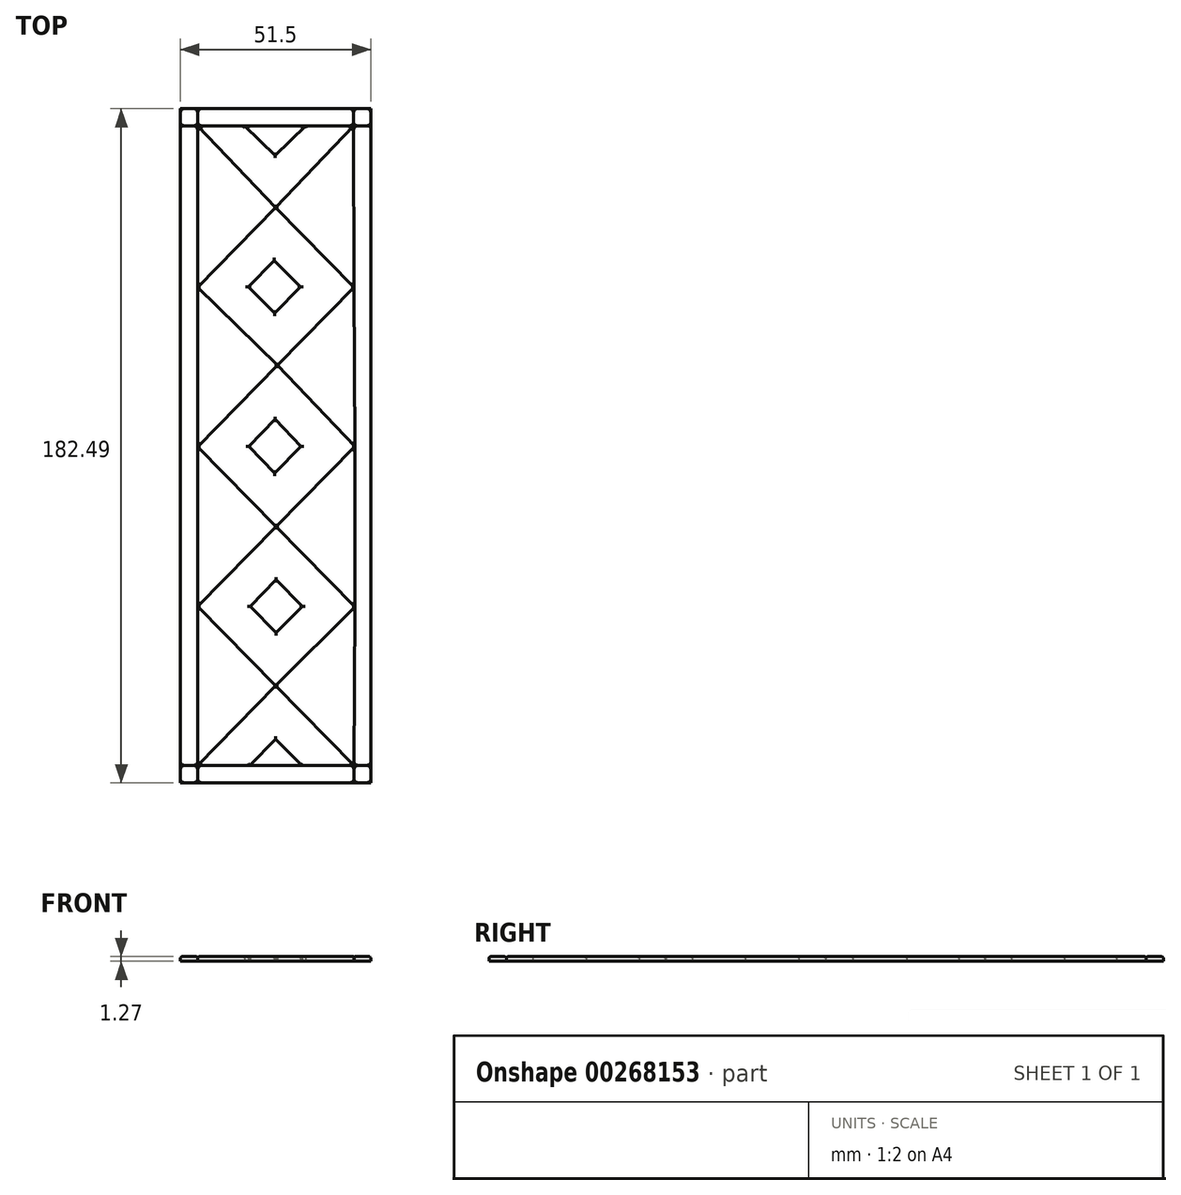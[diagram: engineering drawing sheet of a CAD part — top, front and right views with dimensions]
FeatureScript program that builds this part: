
annotation { "Feature Type Name" : "Feature", "Feature Type Description" : "" }
export const myFeature = defineFeature(function(context is Context, id is Id, definition is map)
    precondition{}
    {
        {
            var Q0;
            Q0=qCreatedBy(makeId("Top.planeOp"),FACE);
            var sketch = newSketch(context, id + "F0", { "sketchPlane" : qUnion([Q0])});
            skLineSegment(sketch, "E0.left", {"start": v(0, 0) * mm, "end": v(0, -4.69) * mm});
            skLineSegment(sketch, "E0.right", {"start": v(51.5, 0) * mm, "end": v(51.5, -4.69) * mm});
            skLineSegment(sketch, "E1.left", {"start": v(0, -182.5) * mm, "end": v(0, -177.8) * mm});
            skLineSegment(sketch, "E1.right", {"start": v(51.5, -182.5) * mm, "end": v(51.5, -177.8) * mm});
            skLineSegment(sketch, "E2.bottom", {"start": v(0, 0) * mm, "end": v(4.69, 0) * mm});
            skLineSegment(sketch, "E2.top", {"start": v(0, -182.5) * mm, "end": v(4.69, -182.5) * mm});
            skLineSegment(sketch, "E3.bottom", {"start": v(46.81, 0) * mm, "end": v(51.5, 0) * mm});
            skLineSegment(sketch, "E3.top", {"start": v(46.93, -182.5) * mm, "end": v(51.61, -182.5) * mm});
            skPoint(sketch, "E4.endSnap0", {"position": v(47.2, -91.38) * mm});
            skLineSegment(sketch, "E5", {"start": v(4.69, -177.8) * mm, "end": v(0, -177.8) * mm});
            skLineSegment(sketch, "E6", {"start": v(46.93, -177.8) * mm, "end": v(4.69, -177.8) * mm});
            skLineSegment(sketch, "E7", {"start": v(46.93, -177.8) * mm, "end": v(51.5, -177.8) * mm});
            skLineSegment(sketch, "E8", {"start": v(4.69, -4.69) * mm, "end": v(4.69, 0) * mm});
            skLineSegment(sketch, "E9", {"start": v(4.69, -177.8) * mm, "end": v(4.69, -182.5) * mm});
            skLineSegment(sketch, "E10", {"start": v(4.69, -48.3) * mm, "end": v(4.69, -4.69) * mm});
            skLineSegment(sketch, "E11", {"start": v(4.69, -91.46) * mm, "end": v(4.69, -48.3) * mm});
            skLineSegment(sketch, "E12", {"start": v(4.69, -134.64) * mm, "end": v(4.69, -91.46) * mm});
            skLineSegment(sketch, "E13", {"start": v(4.69, -177.8) * mm, "end": v(4.69, -134.64) * mm});
            skLineSegment(sketch, "E14", {"start": v(46.93, -177.8) * mm, "end": v(47.18, -134.78) * mm});
            skLineSegment(sketch, "E15", {"start": v(47.2, -91.38) * mm, "end": v(47.18, -134.78) * mm});
            skLineSegment(sketch, "E16", {"start": v(47.2, -91.38) * mm, "end": v(46.93, -48.3) * mm});
            skLineSegment(sketch, "E17", {"start": v(46.81, -4.69) * mm, "end": v(46.93, -48.3) * mm});
            skLineSegment(sketch, "E18", {"start": v(46.81, -4.69) * mm, "end": v(46.81, 0) * mm});
            skLineSegment(sketch, "E19", {"start": v(46.93, -177.8) * mm, "end": v(46.93, -182.5) * mm});
            skLineSegment(sketch, "E20", {"start": v(0, -4.69) * mm, "end": v(0, -177.8) * mm});
            skLineSegment(sketch, "E21", {"start": v(0, -4.69) * mm, "end": v(4.69, -4.69) * mm});
            skLineSegment(sketch, "E22", {"start": v(4.69, -4.69) * mm, "end": v(46.81, -4.69) * mm});
            skLineSegment(sketch, "E23", {"start": v(46.81, -4.69) * mm, "end": v(51.5, -4.69) * mm});
            skLineSegment(sketch, "E24", {"start": v(4.69, 0) * mm, "end": v(46.81, 0) * mm});
            skLineSegment(sketch, "E25", {"start": v(4.69, -182.5) * mm, "end": v(46.93, -182.5) * mm});
            skLineSegment(sketch, "E26", {"start": v(51.5, -177.8) * mm, "end": v(51.5, -4.69) * mm});
            skLineSegment(sketch, "E27", {"start": v(25.6, -84.07) * mm, "end": v(18.45, -91.38) * mm});
            skLineSegment(sketch, "E28", {"start": v(18.45, -91.38) * mm, "end": v(25.5, -98.63) * mm});
            skLineSegment(sketch, "E29", {"start": v(25.5, -98.63) * mm, "end": v(32.62, -91.35) * mm});
            skLineSegment(sketch, "E30", {"start": v(32.62, -91.35) * mm, "end": v(25.6, -84.07) * mm});
            skLineSegment(sketch, "E31", {"start": v(25.39, -41.05) * mm, "end": v(18.4, -48.2) * mm});
            skLineSegment(sketch, "E32", {"start": v(18.4, -48.2) * mm, "end": v(25.52, -55.3) * mm});
            skLineSegment(sketch, "E33", {"start": v(25.52, -55.3) * mm, "end": v(32.47, -48.2) * mm});
            skLineSegment(sketch, "E34", {"start": v(32.47, -48.2) * mm, "end": v(25.39, -41.05) * mm});
            skLineSegment(sketch, "E35", {"start": v(26.21, -69.46) * mm, "end": v(4.69, -48.3) * mm});
            skLineSegment(sketch, "E36", {"start": v(26.21, -69.46) * mm, "end": v(46.93, -48.3) * mm});
            skLineSegment(sketch, "E37", {"start": v(46.93, -48.3) * mm, "end": v(25.8, -26.7) * mm});
            skLineSegment(sketch, "E38", {"start": v(4.69, -48.3) * mm, "end": v(25.8, -26.7) * mm});
            skPoint(sketch, "E39.endSnap0", {"position": v(2.34, -4.69) * mm});
            skLineSegment(sketch, "E40", {"start": v(25.8, -26.7) * mm, "end": v(4.69, -4.69) * mm});
            skLineSegment(sketch, "E41", {"start": v(25.8, -26.7) * mm, "end": v(46.81, -4.69) * mm});
            skLineSegment(sketch, "E42", {"start": v(17.31, -4.69) * mm, "end": v(25.58, -12.61) * mm});
            skLineSegment(sketch, "E43", {"start": v(25.58, -12.61) * mm, "end": v(33.84, -4.69) * mm});
            skLineSegment(sketch, "E44", {"start": v(17.31, -4.69) * mm, "end": v(33.84, -4.69) * mm});
            skLineSegment(sketch, "E45", {"start": v(25.93, -113.12) * mm, "end": v(47.2, -91.38) * mm});
            skLineSegment(sketch, "E46", {"start": v(26.21, -69.46) * mm, "end": v(4.69, -91.46) * mm});
            skLineSegment(sketch, "E47", {"start": v(25.93, -113.12) * mm, "end": v(4.69, -91.46) * mm});
            skLineSegment(sketch, "E48", {"start": v(26.21, -69.46) * mm, "end": v(47.2, -91.38) * mm});
            skLineSegment(sketch, "E49", {"start": v(25.92, -127.5) * mm, "end": v(32.99, -134.72) * mm});
            skLineSegment(sketch, "E50", {"start": v(32.99, -134.72) * mm, "end": v(25.88, -141.87) * mm});
            skLineSegment(sketch, "E51", {"start": v(25.88, -141.87) * mm, "end": v(18.82, -134.67) * mm});
            skLineSegment(sketch, "E52", {"start": v(18.82, -134.67) * mm, "end": v(25.92, -127.5) * mm});
            skLineSegment(sketch, "E53", {"start": v(47.18, -134.78) * mm, "end": v(25.8, -156.22) * mm});
            skLineSegment(sketch, "E54", {"start": v(4.69, -134.64) * mm, "end": v(25.8, -156.22) * mm});
            skLineSegment(sketch, "E55", {"start": v(25.93, -113.12) * mm, "end": v(4.69, -134.64) * mm});
            skLineSegment(sketch, "E56", {"start": v(25.93, -113.12) * mm, "end": v(47.18, -134.78) * mm});
            skLineSegment(sketch, "E57", {"start": v(18.77, -177.8) * mm, "end": v(32.85, -177.8) * mm});
            skLineSegment(sketch, "E58", {"start": v(25.8, -170.61) * mm, "end": v(18.77, -177.8) * mm});
            skLineSegment(sketch, "E59", {"start": v(25.8, -170.61) * mm, "end": v(32.85, -177.8) * mm});
            skLineSegment(sketch, "E60", {"start": v(25.8, -156.22) * mm, "end": v(4.69, -177.8) * mm});
            skLineSegment(sketch, "E61", {"start": v(25.8, -156.22) * mm, "end": v(46.93, -177.8) * mm});
            skSolve(sketch);
        }
        {
            var Q0;
            {var subQ5=sQuery(id+"F0.wireOp",EDGE,"E2.bottom");Q0=makeQuery(id+"F0.imprint","IMPRINT",FACE,{"disambiguationData":[TD([[makeQuery(id+"F0.imprint","IMPRINT",EDGE,{"derivedFrom":subQ5}),-1.0]])]});}
            var Q1;
            {var subQ5=sQuery(id+"F0.wireOp",EDGE,"E3.bottom");Q1=makeQuery(id+"F0.imprint","IMPRINT",FACE,{"disambiguationData":[TD([[makeQuery(id+"F0.imprint","IMPRINT",EDGE,{"derivedFrom":subQ5}),-1.0]])]});}
            var Q2;
            {var subQ5=sQuery(id+"F0.wireOp",EDGE,"E2.top");Q2=makeQuery(id+"F0.imprint","IMPRINT",FACE,{"disambiguationData":[TD([[makeQuery(id+"F0.imprint","IMPRINT",EDGE,{"derivedFrom":subQ5}),1.0]])]});}
            var Q3;
            {var subQ5=sQuery(id+"F0.wireOp",EDGE,"E3.top");Q3=makeQuery(id+"F0.imprint","IMPRINT",FACE,{"disambiguationData":[TD([[makeQuery(id+"F0.imprint","IMPRINT",EDGE,{"derivedFrom":subQ5}),1.0]])]});}
            var Q4;
            Q4=makeQuery(id+"F0.imprint","IMPRINT",FACE,{"disambiguationData":[TD([[makeQuery(id+"F0.imprint","IMPRINT",EDGE,{"derivedFrom":sQuery(id+"F0.wireOp",EDGE,"E42")}),1.0]])]});
            var Q5;
            Q5=makeQuery(id+"F0.imprint","IMPRINT",FACE,{"disambiguationData":[TD([[makeQuery(id+"F0.imprint","IMPRINT",EDGE,{"derivedFrom":sQuery(id+"F0.wireOp",EDGE,"E57")}),1.0]])]});
            extrude(context, id + "F1", {"entities" : qUnion([Q0, Q1, Q2, Q3, Q4, Q5]), "depth" : 1.27 * mm});
        }
        {
            var Q0;
            Q0=makeQuery(id+"F0.imprint","IMPRINT",FACE,{"disambiguationData":[TD([[makeQuery(id+"F0.imprint","IMPRINT",EDGE,{"derivedFrom":sQuery(id+"F0.wireOp",EDGE,"MMf5No5J-Oo0p-8VCI-PQ8X-3j93Xgfx0EA5")}),-1.0]])]});
            var Q1;
            Q1=makeQuery(id+"F0.imprint","IMPRINT",FACE,{"disambiguationData":[TD([[makeQuery(id+"F0.imprint","IMPRINT",EDGE,{"derivedFrom":sQuery(id+"F0.wireOp",EDGE,"IHRdRXlv-QLeJ-v2es-jqY7-16XJjFyKUYhz")}),1.0]])]});
            var Q2;
            {var subQ0=sQuery(id+"F0.wireOp",EDGE,"E12");Q2=makeQuery(id+"F0.imprint","IMPRINT",FACE,{"disambiguationData":[TD([[makeQuery(id+"F0.imprint","IMPRINT",EDGE,{"derivedFrom":subQ0}),-1.0]])]});}
            var Q3;
            {var subQ0=sQuery(id+"F0.wireOp",EDGE,"E15");Q3=makeQuery(id+"F0.imprint","IMPRINT",FACE,{"disambiguationData":[TD([[makeQuery(id+"F0.imprint","IMPRINT",EDGE,{"derivedFrom":subQ0}),-1.0]])]});}
            var Q4;
            Q4=makeQuery(id+"F0.imprint","IMPRINT",FACE,{"disambiguationData":[TD([[makeQuery(id+"F0.imprint","IMPRINT",EDGE,{"derivedFrom":sQuery(id+"F0.wireOp",EDGE,"E11")}),-1.0]])]});
            var Q5;
            Q5=makeQuery(id+"F0.imprint","IMPRINT",FACE,{"disambiguationData":[TD([[makeQuery(id+"F0.imprint","IMPRINT",EDGE,{"derivedFrom":sQuery(id+"F0.wireOp",EDGE,"E16")}),1.0]])]});
            var Q6;
            Q6=makeQuery(id+"F0.imprint","IMPRINT",FACE,{"disambiguationData":[TD([[makeQuery(id+"F0.imprint","IMPRINT",EDGE,{"derivedFrom":sQuery(id+"F0.wireOp",EDGE,"E10")}),-1.0]])]});
            var Q7;
            Q7=makeQuery(id+"F0.imprint","IMPRINT",FACE,{"disambiguationData":[TD([[makeQuery(id+"F0.imprint","IMPRINT",EDGE,{"derivedFrom":sQuery(id+"F0.wireOp",EDGE,"E17")}),-1.0]])]});
            var Q8;
            Q8=makeQuery(id+"F0.imprint","IMPRINT",FACE,{"disambiguationData":[TD([[makeQuery(id+"F0.imprint","IMPRINT",EDGE,{"derivedFrom":sQuery(id+"F0.wireOp",EDGE,"E6")}),1.0]])]});
            var Q9;
            Q9=makeQuery(id+"F0.imprint","IMPRINT",FACE,{"disambiguationData":[TD([[makeQuery(id+"F0.imprint","IMPRINT",EDGE,{"derivedFrom":sQuery(id+"F0.wireOp",EDGE,"E8")}),-1.0]])]});
            var Q10;
            Q10=makeQuery(id+"F0.imprint","IMPRINT",FACE,{"disambiguationData":[TD([[makeQuery(id+"F0.imprint","IMPRINT",EDGE,{"derivedFrom":sQuery(id+"F0.wireOp",EDGE,"E27")}),1.0]])]});
            var Q11;
            Q11=makeQuery(id+"F0.imprint","IMPRINT",FACE,{"disambiguationData":[TD([[makeQuery(id+"F0.imprint","IMPRINT",EDGE,{"derivedFrom":sQuery(id+"F0.wireOp",EDGE,"E31")}),1.0]])]});
            var Q12;
            Q12=makeQuery(id+"F0.imprint","IMPRINT",FACE,{"disambiguationData":[TD([[makeQuery(id+"F0.imprint","IMPRINT",EDGE,{"derivedFrom":sQuery(id+"F0.wireOp",EDGE,"MKFrgVaG-pvdJ-FNnL-0gxz-G25SgSEx1xvv")}),-1.0]])]});
            var Q13;
            Q13=makeQuery(id+"F0.imprint","IMPRINT",FACE,{"disambiguationData":[TD([[makeQuery(id+"F0.imprint","IMPRINT",EDGE,{"derivedFrom":sQuery(id+"F0.wireOp",EDGE,"E49")}),-1.0]])]});
            var Q14;
            Q14=makeQuery(id+"F0.imprint","IMPRINT",FACE,{"disambiguationData":[TD([[makeQuery(id+"F0.imprint","IMPRINT",EDGE,{"derivedFrom":sQuery(id+"F0.wireOp",EDGE,"E13")}),-1.0]])]});
            var Q15;
            Q15=makeQuery(id+"F0.imprint","IMPRINT",FACE,{"disambiguationData":[TD([[makeQuery(id+"F0.imprint","IMPRINT",EDGE,{"derivedFrom":sQuery(id+"F0.wireOp",EDGE,"E14")}),1.0]])]});
            extrude(context, id + "F2", {"entities" : qUnion([Q0, Q1, Q2, Q3, Q4, Q5, Q6, Q7, Q8, Q9, Q10, Q11, Q12, Q13, Q14, Q15]), "depth" : 1.27 * mm});
        }
        {
            var Q0;
            Q0=makeQuery(id+"F2.opExtrude","CAP_FACE",FACE,{"disambiguationData":[OSD([sQuery(id+"F0.wireOp",EDGE,"IHRdRXlv-QLeJ-v2es-jqY7-16XJjFyKUYhz"),sQuery(id+"F0.wireOp",EDGE,"GUx803aM-fHF7-59Js-qxQw-IU8EQgNHGBVG"),sQuery(id+"F0.wireOp",EDGE,"E14")])],"isStart":false});
            var Q1;
            Q1=makeQuery(id+"F2.opExtrude","CAP_FACE",FACE,{"disambiguationData":[OSD([sQuery(id+"F0.wireOp",EDGE,"MMf5No5J-Oo0p-8VCI-PQ8X-3j93Xgfx0EA5"),sQuery(id+"F0.wireOp",EDGE,"MKFrgVaG-pvdJ-FNnL-0gxz-G25SgSEx1xvv"),sQuery(id+"F0.wireOp",EDGE,"E13")])],"isStart":false});
            var Q2;
            Q2=makeQuery(id+"F2.opExtrude","CAP_FACE",FACE,{"disambiguationData":[OSD([sQuery(id+"F0.wireOp",EDGE,"rXMZyDpu-ookE-Mz44-j4OM-uspfrzi3EgYU"),sQuery(id+"F0.wireOp",EDGE,"E15"),sQuery(id+"F0.wireOp",EDGE,"lFyLyK1Y-5PIY-yHM1-0y4J-twjCgxtHjr0K")])],"isStart":false});
            var Q3;
            Q3=makeQuery(id+"F2.opExtrude","CAP_FACE",FACE,{"disambiguationData":[OSD([sQuery(id+"F0.wireOp",EDGE,"rXMZyDpu-ookE-Mz44-j4OM-uspfrzi3EgYU"),sQuery(id+"F0.wireOp",EDGE,"E12"),sQuery(id+"F0.wireOp",EDGE,"cGS4c58A-LVvN-X60S-tC7f-VgP8lSBxNEl8")])],"isStart":false});
            var Q4;
            Q4=makeQuery(id+"F2.opExtrude","CAP_FACE",FACE,{"disambiguationData":[OSD([sQuery(id+"F0.wireOp",EDGE,"E16"),sQuery(id+"F0.wireOp",EDGE,"DMwWLPtW-DNB5-qSH9-V3XZ-fPaCSWvOqiX5"),sQuery(id+"F0.wireOp",EDGE,"TcNrZw8Z-Sjpx-XSh6-N12K-ZUCxzNZfHio8")])],"isStart":false});
            var Q5;
            Q5=makeQuery(id+"F2.opExtrude","CAP_FACE",FACE,{"disambiguationData":[OSD([sQuery(id+"F0.wireOp",EDGE,"E11"),sQuery(id+"F0.wireOp",EDGE,"87clsPCO-xLE4-anr9-w9zI-rIoXzmdd1Mml"),sQuery(id+"F0.wireOp",EDGE,"fyfsV2sT-g7an-vbJt-QfN7-vCYln4SP2rR4")])],"isStart":false});
            var Q6;
            Q6=makeQuery(id+"F2.opExtrude","CAP_FACE",FACE,{"disambiguationData":[OSD([sQuery(id+"F0.wireOp",EDGE,"E17"),sQuery(id+"F0.wireOp",EDGE,"qjLQRWeI-InUO-CIwY-239X-oryCdxkcY3hp"),sQuery(id+"F0.wireOp",EDGE,"qh3aRiE2-Jfkg-7XSm-Rj4r-Xfjd8UzfX591")])],"isStart":false});
            var Q7;
            Q7=makeQuery(id+"F2.opExtrude","CAP_FACE",FACE,{"disambiguationData":[OSD([sQuery(id+"F0.wireOp",EDGE,"E10"),sQuery(id+"F0.wireOp",EDGE,"cLQqAjQk-EXhB-c8nS-kkeQ-Xvv3NVMfrqQR"),sQuery(id+"F0.wireOp",EDGE,"KU5dwC5R-z7BC-oYEm-AJLV-Gyy8FoQ1hqmP")])],"isStart":false});
            var Q8;
            Q8=makeQuery(id+"F2.opExtrude","CAP_EDGE",EDGE,{"disambiguationData":[OSD([sQuery(id+"F0.wireOp",EDGE,"E29")])],"isStart":false});
            var Q9;
            Q9=makeQuery(id+"F2.opExtrude","CAP_EDGE",EDGE,{"disambiguationData":[OSD([sQuery(id+"F0.wireOp",EDGE,"E28")])],"isStart":false});
            var Q10;
            Q10=makeQuery(id+"F2.opExtrude","CAP_EDGE",EDGE,{"disambiguationData":[OSD([sQuery(id+"F0.wireOp",EDGE,"E27")])],"isStart":false});
            var Q11;
            Q11=makeQuery(id+"F2.opExtrude","CAP_EDGE",EDGE,{"disambiguationData":[OSD([sQuery(id+"F0.wireOp",EDGE,"E30")])],"isStart":false});
            var Q12;
            Q12=makeQuery(id+"F2.opExtrude","CAP_EDGE",EDGE,{"disambiguationData":[OSD([sQuery(id+"F0.wireOp",EDGE,"E34")])],"isStart":false});
            var Q13;
            Q13=makeQuery(id+"F2.opExtrude","CAP_EDGE",EDGE,{"disambiguationData":[OSD([sQuery(id+"F0.wireOp",EDGE,"E31")])],"isStart":false});
            var Q14;
            Q14=makeQuery(id+"F2.opExtrude","CAP_EDGE",EDGE,{"disambiguationData":[OSD([sQuery(id+"F0.wireOp",EDGE,"E33")])],"isStart":false});
            var Q15;
            Q15=makeQuery(id+"F2.opExtrude","CAP_EDGE",EDGE,{"disambiguationData":[OSD([sQuery(id+"F0.wireOp",EDGE,"E32")])],"isStart":false});
            var Q16;
            Q16=makeQuery(id+"F1.opExtrude","CAP_EDGE",EDGE,{"disambiguationData":[OSD([sQuery(id+"F0.wireOp",EDGE,"E42")])],"isStart":false});
            var Q17;
            Q17=makeQuery(id+"F1.opExtrude","CAP_EDGE",EDGE,{"disambiguationData":[OSD([sQuery(id+"F0.wireOp",EDGE,"E43")])],"isStart":false});
            var Q18;
            Q18=makeQuery(id+"F1.opExtrude","CAP_FACE",FACE,{"disambiguationData":[OSD([sQuery(id+"F0.wireOp",EDGE,"E42"),sQuery(id+"F0.wireOp",EDGE,"E43"),sQuery(id+"F0.wireOp",EDGE,"E44")])],"isStart":false});
            var Q19;
            Q19=makeQuery(id+"F2.opExtrude","CAP_FACE",FACE,{"disambiguationData":[OSD([sQuery(id+"F0.wireOp",EDGE,"E49"),sQuery(id+"F0.wireOp",EDGE,"E50"),sQuery(id+"F0.wireOp",EDGE,"E51"),sQuery(id+"F0.wireOp",EDGE,"E52")])],"isStart":false});
            var Q20;
            Q20=makeQuery(id+"F1.opExtrude","CAP_FACE",FACE,{"disambiguationData":[OSD([sQuery(id+"F0.wireOp",EDGE,"E57"),sQuery(id+"F0.wireOp",EDGE,"E58"),sQuery(id+"F0.wireOp",EDGE,"E59")])],"isStart":false});
            fillet(context, id + "F3", {"entities" : qUnion([Q0, Q1, Q2, Q3, Q4, Q5, Q6, Q7, Q8, Q9, Q10, Q11, Q12, Q13, Q14, Q15, Q16, Q17, Q18, Q19, Q20]), "radius" : 0.5 * mm, "tangentPropagation" : true, "allowEdgeOverflow" : false});
        }
        {
            var Q0;
            Q0=makeQuery(id+"F2.opExtrude","CAP_FACE",FACE,{"disambiguationData":[OSD([sQuery(id+"F0.wireOp",EDGE,"E8"),sQuery(id+"F0.wireOp",EDGE,"E18"),sQuery(id+"F0.wireOp",EDGE,"E22"),sQuery(id+"F0.wireOp",EDGE,"E24")])],"isStart":false});
            var Q1;
            Q1=makeQuery(id+"F1.opExtrude","CAP_FACE",FACE,{"disambiguationData":[OSD([sQuery(id+"F0.wireOp",EDGE,"E0.left"),sQuery(id+"F0.wireOp",EDGE,"E2.bottom"),sQuery(id+"F0.wireOp",EDGE,"E8"),sQuery(id+"F0.wireOp",EDGE,"E21")])],"isStart":false});
            var Q2;
            Q2=makeQuery(id+"F1.opExtrude","CAP_FACE",FACE,{"disambiguationData":[OSD([sQuery(id+"F0.wireOp",EDGE,"E0.right"),sQuery(id+"F0.wireOp",EDGE,"E3.bottom"),sQuery(id+"F0.wireOp",EDGE,"E18"),sQuery(id+"F0.wireOp",EDGE,"E23")])],"isStart":false});
            var Q3;
            Q3=makeQuery(id+"F1.opExtrude","CAP_FACE",FACE,{"disambiguationData":[OSD([sQuery(id+"F0.wireOp",EDGE,"E1.right"),sQuery(id+"F0.wireOp",EDGE,"E3.top"),sQuery(id+"F0.wireOp",EDGE,"E7"),sQuery(id+"F0.wireOp",EDGE,"E19")])],"isStart":false});
            var Q4;
            Q4=makeQuery(id+"F2.opExtrude","CAP_FACE",FACE,{"disambiguationData":[OSD([sQuery(id+"F0.wireOp",EDGE,"E6"),sQuery(id+"F0.wireOp",EDGE,"E9"),sQuery(id+"F0.wireOp",EDGE,"E19"),sQuery(id+"F0.wireOp",EDGE,"E25")])],"isStart":false});
            var Q5;
            Q5=makeQuery(id+"F1.opExtrude","CAP_FACE",FACE,{"disambiguationData":[OSD([sQuery(id+"F0.wireOp",EDGE,"E1.left"),sQuery(id+"F0.wireOp",EDGE,"E2.top"),sQuery(id+"F0.wireOp",EDGE,"E5"),sQuery(id+"F0.wireOp",EDGE,"E9")])],"isStart":false});
            fillet(context, id + "F4", {"entities" : qUnion([Q0, Q1, Q2, Q3, Q4, Q5]), "radius" : 0.5 * mm, "tangentPropagation" : true, "allowEdgeOverflow" : false});
        }
        {
            var Q0;
            Q0=makeQuery(id+"F0.imprint","IMPRINT",FACE,{"disambiguationData":[TD([[makeQuery(id+"F0.imprint","IMPRINT",EDGE,{"derivedFrom":sQuery(id+"F0.wireOp",EDGE,"E22")}),-1.0]])]});
            var Q1;
            Q1=makeQuery(id+"F0.imprint","IMPRINT",FACE,{"disambiguationData":[TD([[makeQuery(id+"F0.imprint","IMPRINT",EDGE,{"derivedFrom":sQuery(id+"F0.wireOp",EDGE,"cLQqAjQk-EXhB-c8nS-kkeQ-Xvv3NVMfrqQR")}),1.0]])]});
            var Q2;
            Q2=makeQuery(id+"F0.imprint","IMPRINT",FACE,{"disambiguationData":[TD([[makeQuery(id+"F0.imprint","IMPRINT",EDGE,{"derivedFrom":sQuery(id+"F0.wireOp",EDGE,"DMwWLPtW-DNB5-qSH9-V3XZ-fPaCSWvOqiX5")}),-1.0]])]});
            var Q3;
            Q3=makeQuery(id+"F0.imprint","IMPRINT",FACE,{"disambiguationData":[TD([[makeQuery(id+"F0.imprint","IMPRINT",EDGE,{"derivedFrom":sQuery(id+"F0.wireOp",EDGE,"MMf5No5J-Oo0p-8VCI-PQ8X-3j93Xgfx0EA5")}),1.0]])]});
            var Q4;
            Q4=makeQuery(id+"F0.imprint","IMPRINT",FACE,{"disambiguationData":[TD([[makeQuery(id+"F0.imprint","IMPRINT",EDGE,{"derivedFrom":sQuery(id+"F0.wireOp",EDGE,"IHRdRXlv-QLeJ-v2es-jqY7-16XJjFyKUYhz")}),-1.0]])]});
            var Q5;
            Q5=makeQuery(id+"F0.imprint","IMPRINT",FACE,{"disambiguationData":[TD([[makeQuery(id+"F0.imprint","IMPRINT",EDGE,{"derivedFrom":sQuery(id+"F0.wireOp",EDGE,"E5")}),-1.0]])]});
            var Q6;
            Q6=makeQuery(id+"F0.imprint","IMPRINT",FACE,{"disambiguationData":[TD([[makeQuery(id+"F0.imprint","IMPRINT",EDGE,{"derivedFrom":sQuery(id+"F0.wireOp",EDGE,"E7")}),1.0]])]});
            var Q7;
            Q7=makeQuery(id+"F0.imprint","IMPRINT",FACE,{"disambiguationData":[TD([[makeQuery(id+"F0.imprint","IMPRINT",EDGE,{"derivedFrom":sQuery(id+"F0.wireOp",EDGE,"kZVFFZgX-czw2-Alh5-8pL3-di232roHoj8N")}),-1.0]])]});
            var Q8;
            Q8=makeQuery(id+"F0.imprint","IMPRINT",FACE,{"disambiguationData":[TD([[makeQuery(id+"F0.imprint","IMPRINT",EDGE,{"derivedFrom":sQuery(id+"F0.wireOp",EDGE,"E31")}),-1.0]])]});
            var Q9;
            Q9=makeQuery(id+"F0.imprint","IMPRINT",FACE,{"disambiguationData":[TD([[makeQuery(id+"F0.imprint","IMPRINT",EDGE,{"derivedFrom":sQuery(id+"F0.wireOp",EDGE,"E27")}),-1.0]])]});
            var Q10;
            Q10=makeQuery(id+"F0.imprint","IMPRINT",FACE,{"disambiguationData":[TD([[makeQuery(id+"F0.imprint","IMPRINT",EDGE,{"derivedFrom":sQuery(id+"F0.wireOp",EDGE,"E49")}),1.0]])]});
            var Q11;
            {var subQ1=sQuery(id+"F0.wireOp",EDGE,"E58");Q11=makeQuery(id+"F0.imprint","IMPRINT",FACE,{"disambiguationData":[TD([[makeQuery(id+"F0.imprint","IMPRINT",EDGE,{"derivedFrom":subQ1}),-1.0]])]});}
            extrude(context, id + "F5", {"entities" : qUnion([Q0, Q1, Q2, Q3, Q4, Q5, Q6, Q7, Q8, Q9, Q10, Q11]), "depth" : 1.27 * mm});
        }
        {
            var Q0;
            Q0=makeQuery(id+"F5.opExtrude","CAP_FACE",FACE,{"disambiguationData":[OSD([sQuery(id+"F0.wireOp",EDGE,"E22"),sQuery(id+"F0.wireOp",EDGE,"qjLQRWeI-InUO-CIwY-239X-oryCdxkcY3hp"),sQuery(id+"F0.wireOp",EDGE,"KU5dwC5R-z7BC-oYEm-AJLV-Gyy8FoQ1hqmP")])],"isStart":false});
            var Q1;
            Q1=makeQuery(id+"F5.opExtrude","CAP_FACE",FACE,{"disambiguationData":[OSD([sQuery(id+"F0.wireOp",EDGE,"cLQqAjQk-EXhB-c8nS-kkeQ-Xvv3NVMfrqQR"),sQuery(id+"F0.wireOp",EDGE,"qh3aRiE2-Jfkg-7XSm-Rj4r-Xfjd8UzfX591"),sQuery(id+"F0.wireOp",EDGE,"87clsPCO-xLE4-anr9-w9zI-rIoXzmdd1Mml"),sQuery(id+"F0.wireOp",EDGE,"TcNrZw8Z-Sjpx-XSh6-N12K-ZUCxzNZfHio8")])],"isStart":false});
            var Q2;
            Q2=makeQuery(id+"F5.opExtrude","CAP_FACE",FACE,{"disambiguationData":[OSD([sQuery(id+"F0.wireOp",EDGE,"rXMZyDpu-ookE-Mz44-j4OM-uspfrzi3EgYU"),sQuery(id+"F0.wireOp",EDGE,"DMwWLPtW-DNB5-qSH9-V3XZ-fPaCSWvOqiX5"),sQuery(id+"F0.wireOp",EDGE,"fyfsV2sT-g7an-vbJt-QfN7-vCYln4SP2rR4"),sQuery(id+"F0.wireOp",EDGE,"lFyLyK1Y-5PIY-yHM1-0y4J-twjCgxtHjr0K")])],"isStart":false});
            var Q3;
            Q3=makeQuery(id+"F5.opExtrude","CAP_FACE",FACE,{"disambiguationData":[OSD([sQuery(id+"F0.wireOp",EDGE,"rXMZyDpu-ookE-Mz44-j4OM-uspfrzi3EgYU"),sQuery(id+"F0.wireOp",EDGE,"MMf5No5J-Oo0p-8VCI-PQ8X-3j93Xgfx0EA5"),sQuery(id+"F0.wireOp",EDGE,"GUx803aM-fHF7-59Js-qxQw-IU8EQgNHGBVG"),sQuery(id+"F0.wireOp",EDGE,"cGS4c58A-LVvN-X60S-tC7f-VgP8lSBxNEl8")])],"isStart":false});
            var Q4;
            Q4=makeQuery(id+"F5.opExtrude","CAP_FACE",FACE,{"disambiguationData":[OSD([sQuery(id+"F0.wireOp",EDGE,"IHRdRXlv-QLeJ-v2es-jqY7-16XJjFyKUYhz"),sQuery(id+"F0.wireOp",EDGE,"MKFrgVaG-pvdJ-FNnL-0gxz-G25SgSEx1xvv"),sQuery(id+"F0.wireOp",EDGE,"E6")])],"isStart":false});
            var Q5;
            Q5=makeQuery(id+"F5.opExtrude","CAP_EDGE",EDGE,{"disambiguationData":[OSD([sQuery(id+"F0.wireOp",EDGE,"TTTgAY0Y-4ibG-fORp-3PHE-J1eBD3dRwHgp"),sQuery(id+"F0.wireOp",EDGE,"10AczeKA-ev1X-eVkn-KtVd-szyNO4J1XlUk"),sQuery(id+"F0.wireOp",EDGE,"ranzLWVo-dyIm-a4VB-tWad-Z6Jlyx0ZF3eC")])],"isStart":false});
            var Q6;
            Q6=makeQuery(id+"F5.opExtrude","CAP_EDGE",EDGE,{"disambiguationData":[OSD([sQuery(id+"F0.wireOp",EDGE,"kZVFFZgX-czw2-Alh5-8pL3-di232roHoj8N"),sQuery(id+"F0.wireOp",EDGE,"lBiX9b55-Io1h-x8PR-40tF-HHdKPiM466Ld"),sQuery(id+"F0.wireOp",EDGE,"VDp8MpQw-teJY-W9zc-qyi6-sDfQ9q4jybxq")])],"isStart":false});
            var Q7;
            Q7=makeQuery(id+"F5.opExtrude","CAP_EDGE",EDGE,{"disambiguationData":[OSD([sQuery(id+"F0.wireOp",EDGE,"Celpjyum-c6aV-4rhz-ljmn-gYGRuUpbnUD6"),sQuery(id+"F0.wireOp",EDGE,"cnv8ARII-h3Yy-ozQu-olxj-4SHU1OzJZRZK"),sQuery(id+"F0.wireOp",EDGE,"WolOntlM-ufrX-rn55-o4EH-SSGm71N5Bkpu")])],"isStart":false});
            var Q8;
            Q8=makeQuery(id+"F5.opExtrude","CAP_EDGE",EDGE,{"disambiguationData":[OSD([sQuery(id+"F0.wireOp",EDGE,"7ALOyG6m-Rzc4-yNME-kMFY-bujnrLPdKhah"),sQuery(id+"F0.wireOp",EDGE,"B6t2ZTu5-IcsM-qhxP-ARks-wSL9V69IWJHq"),sQuery(id+"F0.wireOp",EDGE,"VPNVlkV1-Lgyp-GUOQ-PYls-mq5QhlvyemB7")])],"isStart":false});
            var Q9;
            Q9=makeQuery(id+"F5.opExtrude","CAP_EDGE",EDGE,{"disambiguationData":[OSD([sQuery(id+"F0.wireOp",EDGE,"E29")])],"isStart":false});
            var Q10;
            Q10=makeQuery(id+"F5.opExtrude","CAP_EDGE",EDGE,{"disambiguationData":[OSD([sQuery(id+"F0.wireOp",EDGE,"E28")])],"isStart":false});
            var Q11;
            Q11=makeQuery(id+"F5.opExtrude","CAP_EDGE",EDGE,{"disambiguationData":[OSD([sQuery(id+"F0.wireOp",EDGE,"E27")])],"isStart":false});
            var Q12;
            Q12=makeQuery(id+"F5.opExtrude","CAP_EDGE",EDGE,{"disambiguationData":[OSD([sQuery(id+"F0.wireOp",EDGE,"E30")])],"isStart":false});
            var Q13;
            Q13=makeQuery(id+"F5.opExtrude","CAP_EDGE",EDGE,{"disambiguationData":[OSD([sQuery(id+"F0.wireOp",EDGE,"E37")])],"isStart":false});
            var Q14;
            Q14=makeQuery(id+"F5.opExtrude","CAP_EDGE",EDGE,{"disambiguationData":[OSD([sQuery(id+"F0.wireOp",EDGE,"E38")])],"isStart":false});
            var Q15;
            Q15=makeQuery(id+"F5.opExtrude","CAP_EDGE",EDGE,{"disambiguationData":[OSD([sQuery(id+"F0.wireOp",EDGE,"E36")])],"isStart":false});
            var Q16;
            Q16=makeQuery(id+"F5.opExtrude","CAP_EDGE",EDGE,{"disambiguationData":[OSD([sQuery(id+"F0.wireOp",EDGE,"E35")])],"isStart":false});
            var Q17;
            Q17=makeQuery(id+"F5.opExtrude","CAP_EDGE",EDGE,{"disambiguationData":[OSD([sQuery(id+"F0.wireOp",EDGE,"E47")])],"isStart":false});
            var Q18;
            Q18=makeQuery(id+"F5.opExtrude","CAP_EDGE",EDGE,{"disambiguationData":[OSD([sQuery(id+"F0.wireOp",EDGE,"E45")])],"isStart":false});
            var Q19;
            Q19=makeQuery(id+"F5.opExtrude","CAP_EDGE",EDGE,{"disambiguationData":[OSD([sQuery(id+"F0.wireOp",EDGE,"E48")])],"isStart":false});
            var Q20;
            Q20=makeQuery(id+"F5.opExtrude","CAP_EDGE",EDGE,{"disambiguationData":[OSD([sQuery(id+"F0.wireOp",EDGE,"E46")])],"isStart":false});
            var Q21;
            Q21=makeQuery(id+"F5.opExtrude","CAP_EDGE",EDGE,{"disambiguationData":[OSD([sQuery(id+"F0.wireOp",EDGE,"E20")])],"isStart":false});
            var Q22;
            Q22=makeQuery(id+"F5.opExtrude","CAP_EDGE",EDGE,{"disambiguationData":[OSD([sQuery(id+"F0.wireOp",EDGE,"E26")])],"isStart":false});
            var Q23;
            Q23=makeQuery(id+"F5.opExtrude","CAP_EDGE",EDGE,{"disambiguationData":[OSD([sQuery(id+"F0.wireOp",EDGE,"E23")])],"isStart":false});
            var Q24;
            Q24=makeQuery(id+"F5.opExtrude","CAP_EDGE",EDGE,{"disambiguationData":[OSD([sQuery(id+"F0.wireOp",EDGE,"E17")])],"isStart":false});
            var Q25;
            Q25=makeQuery(id+"F5.opExtrude","CAP_EDGE",EDGE,{"disambiguationData":[OSD([sQuery(id+"F0.wireOp",EDGE,"E7")])],"isStart":false});
            var Q26;
            Q26=makeQuery(id+"F5.opExtrude","CAP_EDGE",EDGE,{"disambiguationData":[OSD([sQuery(id+"F0.wireOp",EDGE,"E14")])],"isStart":false});
            var Q27;
            Q27=makeQuery(id+"F5.opExtrude","CAP_EDGE",EDGE,{"disambiguationData":[OSD([sQuery(id+"F0.wireOp",EDGE,"E12"),sQuery(id+"F0.wireOp",EDGE,"E13")])],"isStart":false});
            var Q28;
            Q28=makeQuery(id+"F5.opExtrude","CAP_EDGE",EDGE,{"disambiguationData":[OSD([sQuery(id+"F0.wireOp",EDGE,"E5")])],"isStart":false});
            var Q29;
            Q29=makeQuery(id+"F5.opExtrude","CAP_EDGE",EDGE,{"disambiguationData":[OSD([sQuery(id+"F0.wireOp",EDGE,"E21")])],"isStart":false});
            var Q30;
            Q30=makeQuery(id+"F5.opExtrude","CAP_EDGE",EDGE,{"disambiguationData":[OSD([sQuery(id+"F0.wireOp",EDGE,"E34")])],"isStart":false});
            var Q31;
            Q31=makeQuery(id+"F5.opExtrude","CAP_EDGE",EDGE,{"disambiguationData":[OSD([sQuery(id+"F0.wireOp",EDGE,"E33")])],"isStart":false});
            var Q32;
            Q32=makeQuery(id+"F5.opExtrude","CAP_EDGE",EDGE,{"disambiguationData":[OSD([sQuery(id+"F0.wireOp",EDGE,"E32")])],"isStart":false});
            var Q33;
            Q33=makeQuery(id+"F5.opExtrude","CAP_EDGE",EDGE,{"disambiguationData":[OSD([sQuery(id+"F0.wireOp",EDGE,"E31")])],"isStart":false});
            var Q34;
            Q34=makeQuery(id+"F5.opExtrude","CAP_FACE",FACE,{"disambiguationData":[OSD([sQuery(id+"F0.wireOp",EDGE,"E49"),sQuery(id+"F0.wireOp",EDGE,"E50"),sQuery(id+"F0.wireOp",EDGE,"E51"),sQuery(id+"F0.wireOp",EDGE,"E52"),sQuery(id+"F0.wireOp",EDGE,"E53"),sQuery(id+"F0.wireOp",EDGE,"E54"),sQuery(id+"F0.wireOp",EDGE,"E55"),sQuery(id+"F0.wireOp",EDGE,"E56")])],"isStart":false});
            fillet(context, id + "F6", {"entities" : qUnion([Q0, Q1, Q2, Q3, Q4, Q5, Q6, Q7, Q8, Q9, Q10, Q11, Q12, Q13, Q14, Q15, Q16, Q17, Q18, Q19, Q20, Q21, Q22, Q23, Q24, Q25, Q26, Q27, Q28, Q29, Q30, Q31, Q32, Q33, Q34]), "radius" : 0.5 * mm, "tangentPropagation" : true, "allowEdgeOverflow" : false});
        }
    });
